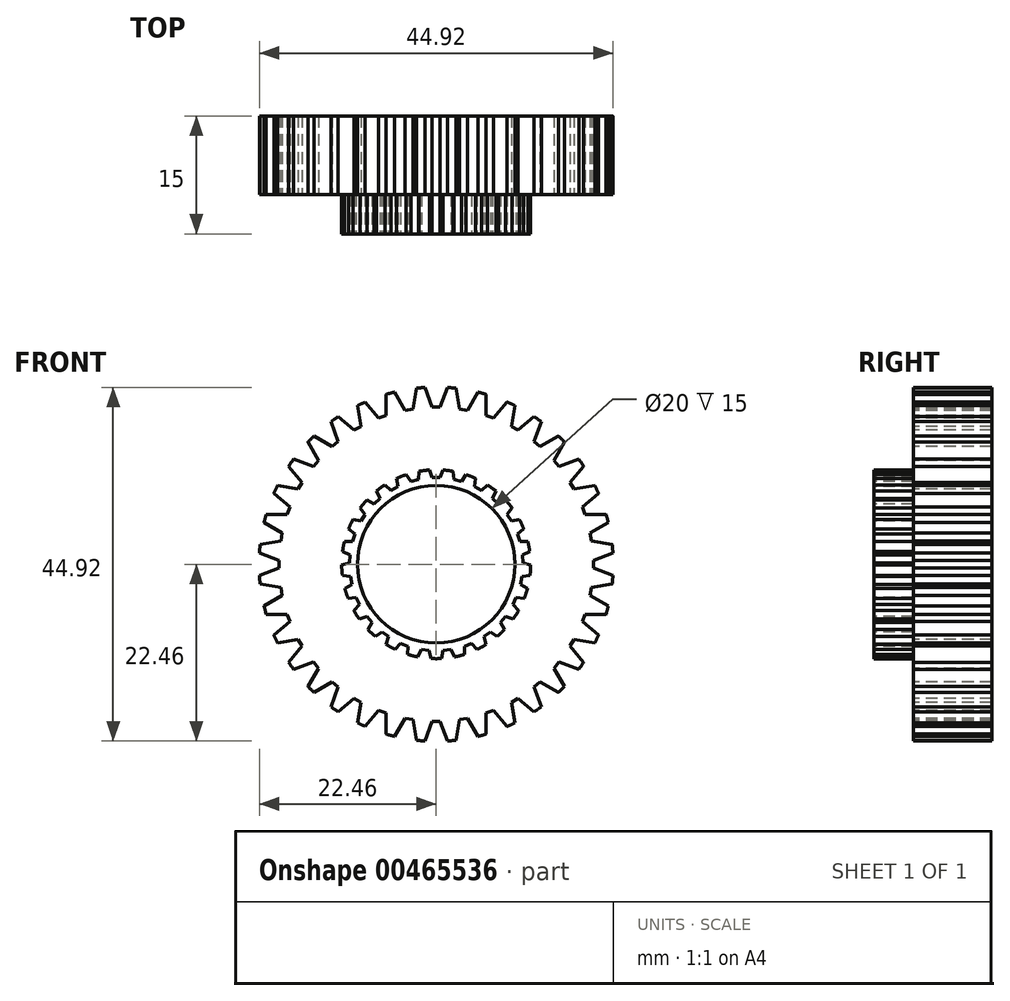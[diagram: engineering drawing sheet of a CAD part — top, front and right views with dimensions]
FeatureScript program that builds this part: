
annotation { "Feature Type Name" : "Feature", "Feature Type Description" : "" }
export const myFeature = defineFeature(function(context is Context, id is Id, definition is map)
    precondition{}
    {
        {
            var Q0;
            Q0=qCreatedBy(makeId("Front.planeOp"),FACE);
            var sketch = newSketch(context, id + "F0", { "sketchPlane" : qUnion([Q0])});
            skCircle(sketch, "E0", {"center": v(0, 0) * mm, "radius": 22.5 * mm});
            skCircle(sketch, "E1", {"center": v(0, 0) * mm, "radius": 10 * mm});
            skSolve(sketch);
        }
        {
            var Q0;
            Q0=makeQuery(id+"F0.imprint","IMPRINT",FACE,{"disambiguationData":[TD([[makeQuery(id+"F0.imprint","IMPRINT",EDGE,{"derivedFrom":sQuery(id+"F0.wireOp",EDGE,"E0")}),1.0]])]});
            extrude(context, id + "F1", {"entities" : qUnion([Q0]), "depth" : 10 * mm});
        }
        {
            var Q0;
            Q0=makeQuery(id+"F1.opExtrude","CAP_FACE",FACE,{"disambiguationData":[OSD([sQuery(id+"F0.wireOp",EDGE,"E0"),sQuery(id+"F0.wireOp",EDGE,"E1")])],"isStart":false});
            var sketch = newSketch(context, id + "F2", { "sketchPlane" : qUnion([Q0])});
            skLineSegment(sketch, "E2", {"start": v(0, 19.95) * mm, "end": v(-0.5, 19.95) * mm});
            skLineSegment(sketch, "E3", {"start": v(0, 19.95) * mm, "end": v(0.5, 19.95) * mm});
            skLineSegment(sketch, "E4", {"start": v(0.5, 19.95) * mm, "end": v(1.41, 22.46) * mm});
            skLineSegment(sketch, "E5", {"start": v(0, 22.5) * mm, "end": v(0, 0) * mm, "construction": true});
            skLineSegment(sketch, "E6", {"start": v(-0.5, 19.95) * mm, "end": v(-1.41, 22.46) * mm});
            skCircle(sketch, "E7", {"center": v(0, 0) * mm, "radius": 12 * mm});
            skSolve(sketch);
        }
        {
            var Q0;
            Q0=makeQuery(id+"F2.imprint","IMPRINT",FACE,{"disambiguationData":[TD([[makeQuery(id+"F2.imprint","IMPRINT",EDGE,{"derivedFrom":sQuery(id+"F2.wireOp",EDGE,"E2")}),-1.0]])]});
            extrude(context, id + "F3", {"entities" : qUnion([Q0]), "operationType" : NewBodyOperationType.REMOVE, "oppositeDirection" : true, "depth" : 25 * mm});
        }
        {
            var Q0;
            Q0=makeQuery(id+"F3.boolean.opBoolean","COPY",FACE,{"derivedFrom":makeQuery(id+"F3.opExtrude","SWEPT_FACE",FACE,{"disambiguationData":[OSD([sQuery(id+"F2.wireOp",EDGE,"E6")])]})});
            var Q1;
            Q1=makeQuery(id+"F3.boolean.opBoolean","COPY",FACE,{"derivedFrom":makeQuery(id+"F3.opExtrude","SWEPT_FACE",FACE,{"disambiguationData":[OSD([sQuery(id+"F2.wireOp",EDGE,"E2"),sQuery(id+"F2.wireOp",EDGE,"E3")])]})});
            var Q2;
            Q2=makeQuery(id+"F3.boolean.opBoolean","COPY",FACE,{"derivedFrom":makeQuery(id+"F3.opExtrude","SWEPT_FACE",FACE,{"disambiguationData":[OSD([sQuery(id+"F2.wireOp",EDGE,"E4")])]})});
            var Q3;
            Q3=makeQuery(id+"F1.opExtrude","SWEPT_FACE",FACE,{"disambiguationData":[OSD([sQuery(id+"F0.wireOp",EDGE,"E0")])]});
            circularPattern(context, id + "F4", {"patternType" : PatternType.FACE, "faces" : qUnion([Q0, Q1, Q2]), "axis" : qUnion([Q3]), "angle" : 360 * degree, "instanceCount" : 36, "equalSpace" : true});
        }
        {
            var Q0;
            Q0=makeQuery(id+"F2.imprint","IMPRINT",FACE,{"disambiguationData":[TD([[makeQuery(id+"F2.imprint","IMPRINT",EDGE,{"derivedFrom":sQuery(id+"F2.wireOp",EDGE,"E7")}),1.0]])]});
            extrude(context, id + "F5", {"entities" : qUnion([Q0]), "operationType" : NewBodyOperationType.ADD, "depth" : 5 * mm});
        }
        {
            var Q0;
            Q0=makeQuery(id+"F5.opExtrude","CAP_FACE",FACE,{"disambiguationData":[OSD([sQuery(id+"F0.wireOp",EDGE,"E1"),sQuery(id+"F2.wireOp",EDGE,"E7")])],"isStart":false});
            var sketch = newSketch(context, id + "F6", { "sketchPlane" : qUnion([Q0])});
            skLineSegment(sketch, "E8", {"start": v(0, 0) * mm, "end": v(0, 12) * mm, "construction": true});
            skLineSegment(sketch, "E9", {"start": v(0, 12) * mm, "end": v(0, 11) * mm, "construction": true});
            skLineSegment(sketch, "E10", {"start": v(0, 11) * mm, "end": v(-0.5, 11) * mm});
            skLineSegment(sketch, "E11", {"start": v(0, 11) * mm, "end": v(0.5, 11) * mm});
            skLineSegment(sketch, "E12", {"start": v(-0.5, 11) * mm, "end": v(-0.85, 11.97) * mm});
            skLineSegment(sketch, "E13", {"start": v(0.5, 11) * mm, "end": v(0.85, 11.97) * mm});
            skSolve(sketch);
        }
        {
            var Q0;
            Q0=makeQuery(id+"F6.imprint","IMPRINT",FACE,{"disambiguationData":[TD([[makeQuery(id+"F6.imprint","IMPRINT",EDGE,{"derivedFrom":sQuery(id+"F6.wireOp",EDGE,"E10")}),-1.0]])]});
            extrude(context, id + "F7", {"entities" : qUnion([Q0]), "operationType" : NewBodyOperationType.REMOVE, "oppositeDirection" : true, "depth" : 5 * mm});
        }
        {
            var Q0;
            Q0=makeQuery(id+"F7.boolean.opBoolean","COPY",FACE,{"derivedFrom":makeQuery(id+"F7.opExtrude","SWEPT_FACE",FACE,{"disambiguationData":[OSD([sQuery(id+"F6.wireOp",EDGE,"E12")])]})});
            var Q1;
            Q1=makeQuery(id+"F7.boolean.opBoolean","COPY",FACE,{"derivedFrom":makeQuery(id+"F7.opExtrude","SWEPT_FACE",FACE,{"disambiguationData":[OSD([sQuery(id+"F6.wireOp",EDGE,"E10"),sQuery(id+"F6.wireOp",EDGE,"E11")])]})});
            var Q2;
            Q2=makeQuery(id+"F7.boolean.opBoolean","COPY",FACE,{"derivedFrom":makeQuery(id+"F7.opExtrude","SWEPT_FACE",FACE,{"disambiguationData":[OSD([sQuery(id+"F6.wireOp",EDGE,"E13")])]})});
            var Q3;
            Q3=makeQuery(id+"F5.opExtrude","SWEPT_FACE",FACE,{"disambiguationData":[OSD([sQuery(id+"F2.wireOp",EDGE,"E7")])]});
            circularPattern(context, id + "F8", {"patternType" : PatternType.FACE, "faces" : qUnion([Q0, Q1, Q2]), "axis" : qUnion([Q3]), "angle" : 360 * degree, "instanceCount" : 25, "equalSpace" : true});
        }
    });
